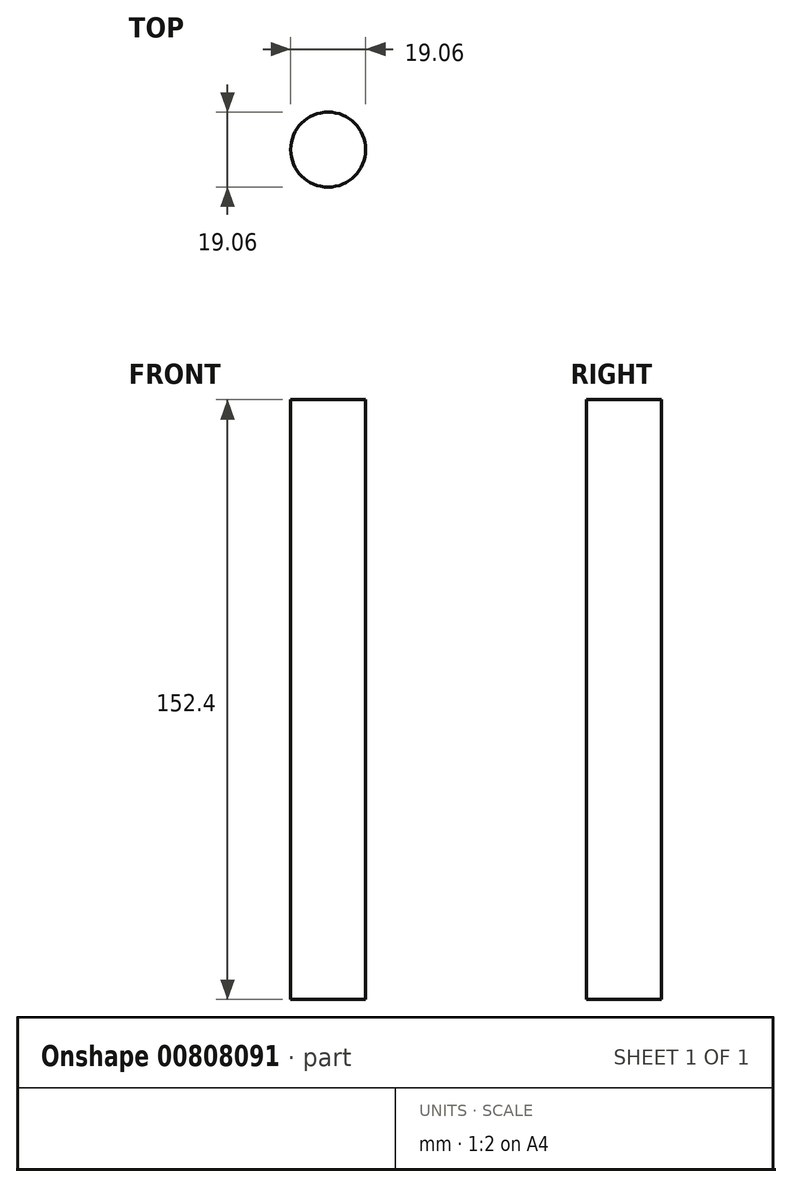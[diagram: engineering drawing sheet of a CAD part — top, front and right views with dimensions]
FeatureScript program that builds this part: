
annotation { "Feature Type Name" : "Feature", "Feature Type Description" : "" }
export const myFeature = defineFeature(function(context is Context, id is Id, definition is map)
    precondition{}
    {
        {
            var Q0;
            Q0=qCreatedBy(makeId("Top.planeOp"),FACE);
            var sketch = newSketch(context, id + "F0", { "sketchPlane" : qUnion([Q0])});
            skCircle(sketch, "E0", {"center": v(0, 0) * mm, "radius": 9.53 * mm});
            skSolve(sketch);
        }
        {
            var Q0;
            Q0=makeQuery(id+"F0.imprint","IMPRINT",FACE,{"disambiguationData":[TD([[makeQuery(id+"F0.imprint","IMPRINT",EDGE,{"derivedFrom":sQuery(id+"F0.wireOp",EDGE,"E0")}),1.0]])]});
            extrude(context, id + "F1", {"entities" : qUnion([Q0]), "oppositeDirection" : true, "depth" : 152.4 * mm, "offsetDistance" : 25.4 * mm});
        }
    });
